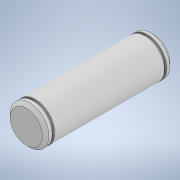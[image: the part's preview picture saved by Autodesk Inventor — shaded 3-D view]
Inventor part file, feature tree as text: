
AUTODESK INVENTOR PART (.ipt)
format: ipt  version: 2022 (Build 260153000, 153)  size: 135,168 bytes
history: native  units: mm
features: sketch x2, projected_geometry x2, revolve x1
ambient origin geometry x8: Origin, YZ Plane, XZ Plane, XY Plane, X Axis, Y Axis, Z Axis, Center Point
bodies: Solid1 (feature_tree)
feature tree (5):
  revolve  "Revolution1"  [1 undecoded]
  sketch  "Sketch3"  dims[d2=0.7mm d3=0.5mm d7=2.0mm d8=1.0mm d9=1.0mm d10=90.0deg]
  sketch  "Sketch1"  dims[d0=6.0mm d1=17.0mm]
  projected_geometry  "Projected Loop1"
  projected_geometry  "Projected Loop2"
note: 1 required parameter value undecoded (feature->parameter linkage not recoverable at this tier; creation-order binding heuristic only, values carry confidence <= 0.55)
